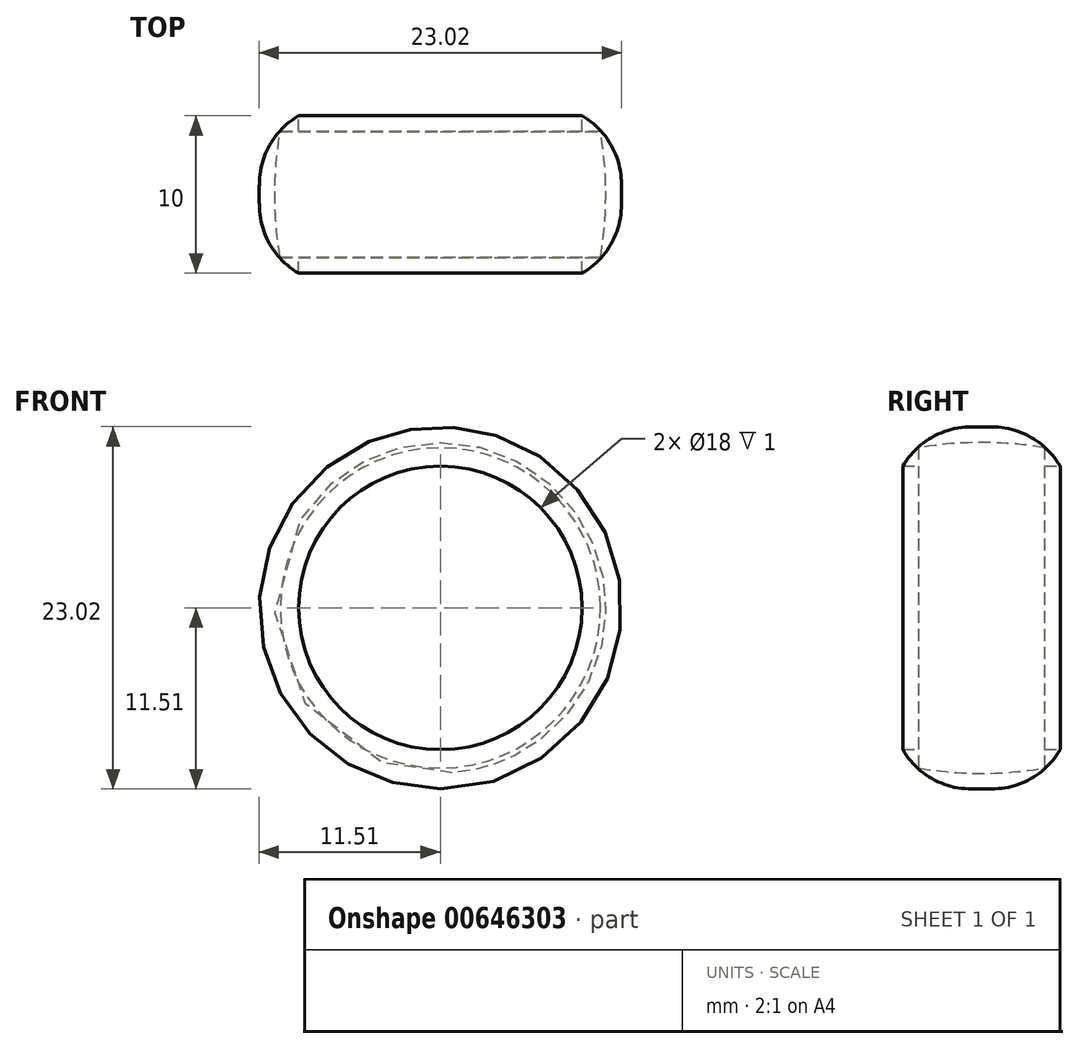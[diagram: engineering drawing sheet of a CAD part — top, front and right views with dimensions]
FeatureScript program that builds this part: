
annotation { "Feature Type Name" : "Feature", "Feature Type Description" : "" }
export const myFeature = defineFeature(function(context is Context, id is Id, definition is map)
    precondition{}
    {
        {
            var Q0;
            Q0=qCreatedBy(makeId("Top.planeOp"),FACE);
            var sketch = newSketch(context, id + "F0", { "sketchPlane" : qUnion([Q0])});
            skLineSegment(sketch, "E0", {"start": v(0, 0) * mm, "end": v(-9, 0) * mm, "construction": true});
            skLineSegment(sketch, "E1", {"start": v(-9, 5) * mm, "end": v(-9, -5) * mm});
            skLineSegment(sketch, "E2", {"start": v(-9, 5) * mm, "end": v(-11, 5) * mm});
            skLineSegment(sketch, "E3", {"start": v(-9, -5) * mm, "end": v(-11, -5) * mm});
            skArc(sketch, "E4", {"start": v(-11, 5) * mm, "mid": v(-11.5, 0) * mm, "end": v(-11, -5) * mm});
            skLineSegment(sketch, "E5", {"start": v(0, 0) * mm, "end": v(0, -13.47) * mm, "construction": true});
            skSolve(sketch);
        }
        {
            var Q0;
            Q0=makeQuery(id+"F0.imprint","IMPRINT",FACE,{"disambiguationData":[TD([[makeQuery(id+"F0.imprint","IMPRINT",EDGE,{"derivedFrom":sQuery(id+"F0.wireOp",EDGE,"E1")}),-1.0]])]});
            var Q1;
            Q1=sQuery(id+"F0.wireOp",EDGE,"E5");
            revolve(context, id + "F1", {"entities" : qUnion([Q0]), "axis" : qUnion([Q1]), "revolveType" : RevolveType.FULL});
        }
        {
            var Q0;
            Q0=makeQuery(id+"F1.opRevolve","SWEPT_FACE",FACE,{"disambiguationData":[OSD([sQuery(id+"F0.wireOp",EDGE,"E1")])]});
            shell(context, id + "F2", {"entities" : qUnion([Q0]), "thickness" : 1 * mm});
        }
        {
            var Q0;
            Q0=makeQuery(id+"F1.opRevolve","SWEPT_FACE",FACE,{"disambiguationData":[OSD([sQuery(id+"F0.wireOp",EDGE,"E4")])]});
            fillet(context, id + "F3", {"entities" : qUnion([Q0]), "radius" : 5 * mm, "tangentPropagation" : true, "allowEdgeOverflow" : false});
        }
    });
